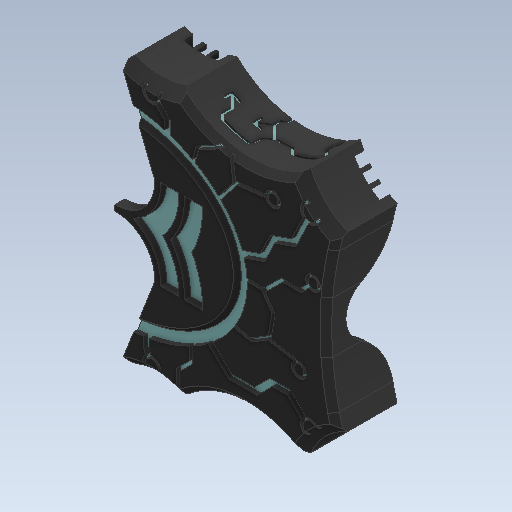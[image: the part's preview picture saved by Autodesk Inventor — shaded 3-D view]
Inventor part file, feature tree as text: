
AUTODESK INVENTOR PART (.ipt)
format: ipt  version: 2020 (Build 240168000, 168)  size: 1,965,056 bytes
history: native  units: mm
features: reference x74, projected_geometry x20, sketch x19, extrude x17, plane x6, other x6, fillet x5, chamfer x5, mirror x2, emboss x2
ambient origin geometry x8: Origin, YZ Plane, XZ Plane, XY Plane, X Axis, Y Axis, Z Axis, Center Point
bodies: Solid1 (feature_tree)
feature tree (156):
  extrude  "Extrusion1"  Depth=70.0mm
  extrude  "Extrusion4"  Depth=29.189217mm
  extrude  "Extrusion7"  Depth=20.0mm TaperAngle=0.0deg
  extrude  "Extrusion8"  Depth=36.552mm TaperAngle=0.0deg
  extrude  "Extrusion9"  Depth=20.0mm
  plane  "Work Plane2"
  mirror  "Mirror1"
  extrude  "Extrusion10"  Depth=26.0mm
  fillet  "Fillet3"  Radius=15.25mm
  fillet  "Fillet4"  Radius=35.5mm
  plane  "Work Plane3"
  extrude  "Extrusion11"  Depth=26.5mm TaperAngle=0.0deg
  plane  "Work Plane4"
  extrude  "Extrusion12"  Depth=46.75mm
  plane  "Work Plane5"
  extrude  "Extrusion14"  Depth=1.6mm TaperAngle=0.0deg
  fillet  "Fillet5"  Radius=78.75mm
  fillet  "Fillet6"  Radius=3.0mm
  fillet  "Fillet8"  Radius=5.0mm
  extrude  "Extrusion15"  Depth=8.0mm TaperAngle=0.0deg
  plane  "Work Plane6"
  extrude  "Extrusion17"  Depth=5.6mm
  emboss  "Emboss1"
  chamfer  "Chamfer3"  Distance=2.0mm
  chamfer  "Chamfer4"  Distance=12.25mm
  extrude  "Extrusion18"  Depth=2.0mm
  extrude  "Extrusion19"  Depth=45.0mm
  extrude  "Extrusion20"  Depth=50.0mm
  extrude  "Extrusion21"  Depth=2.0mm TaperAngle=0.0deg
  chamfer  "Chamfer5"  Distance=7.0mm
  extrude  "Extrusion22"  Depth=7.0mm
  extrude  "Extrusion23"  Depth=7.0mm
  chamfer  "Chamfer8"  Distance=7.0mm
  plane  "Work Plane8"
  emboss  "Emboss5"
  mirror  "Mirror2"
  chamfer  "Chamfer9"  Distance=9.5mm
  sketch  "Sketch1"  dims[d0=10.0mm d1=0.0mm d6=70.0mm]
  reference  "Reference1"
  reference  "Reference2"
  reference  "Reference3"
  reference  "Reference4"
  reference  "Reference5"
  reference  "Reference6"
  reference  "Reference7"
  reference  "Reference8"
  reference  "Reference9"
  reference  "Reference10"
  reference  "Reference11"
  reference  "Reference12"
  reference  "Reference13"
  reference  "Reference14"
  reference  "Reference15"
  reference  "Reference16"
  reference  "Reference17"
  reference  "Reference18"
  reference  "Reference19"
  reference  "Reference20"
  reference  "Reference21"
  reference  "Reference22"
  reference  "Reference23"
  reference  "Reference24"
  reference  "Reference25"
  reference  "Reference26"
  reference  "Reference27"
  reference  "Reference28"
  reference  "Reference29"
  reference  "Reference30"
  reference  "Reference31"
  reference  "Reference32"
  reference  "Reference33"
  reference  "Reference34"
  reference  "Reference35"
  reference  "Reference36"
  reference  "Reference37"
  reference  "Reference38"
  reference  "Reference39"
  reference  "Reference40"
  reference  "Reference41"
  reference  "Reference42"
  reference  "Reference43"
  reference  "Reference44"
  reference  "Reference45"
  reference  "Reference46"
  reference  "Reference47"
  reference  "Reference48"
  reference  "Reference49"
  reference  "Reference50"
  reference  "Reference51"
  reference  "Reference52"
  reference  "Reference53"
  reference  "Reference54"
  reference  "Reference55"
  reference  "Reference56"
  reference  "Reference57"
  reference  "Reference58"
  reference  "Reference59"
  reference  "Reference60"
  reference  "Reference61"
  reference  "Reference62"
  sketch  "Sketch5"  dims[d7=29.189217mm d8=29.189217mm]
  sketch  "Sketch8"  dims[d9=5.0mm d10=0.0mm d21=20.0mm d22=0.0mm]
  projected_geometry  "Projected Loop39"
  sketch  "Sketch9"  dims[d23=4.0mm d24=0.0mm d25=36.552mm d26=0.0mm]
  reference  "Reference110"
  projected_geometry  "Projected Loop40"
  sketch  "Sketch10"  dims[d27=10.0mm d28=20.0mm]
  projected_geometry  "Projected Loop41"
  sketch  "Sketch11"  dims[d29=20.0mm d30=0.0mm d31=26.0mm d32=15.25mm d33=35.5mm d34=0.0mm]
  projected_geometry  "Projected Loop42"
  sketch  "Sketch12"  dims[d35=5.0mm d36=0.0mm d39=26.5mm d40=0.0mm]
  reference  "Reference111"
  reference  "Reference112"
  reference  "Reference113"
  sketch  "Sketch14"  dims[d41=26.0mm d42=46.75mm]
  projected_geometry  "Projected Loop43"
  projected_geometry  "Projected Loop44"
  sketch  "Sketch16"  dims[d44=5.0mm d45=1.6mm d46=0.0mm d250=78.75mm d251=0.0mm d253=3.0mm d254=0.0mm]
  sketch  "Sketch17"  dims[d255=3.0mm d256=2.0mm d257=45.0deg]
  reference  "Reference114"
  reference  "Reference115"
  reference  "Reference116"
  reference  "Reference117"
  reference  "Reference118"
  reference  "Reference119"
  reference  "Reference120"
  reference  "Reference121"
  sketch  "Sketch19"  dims[d258=5.0mm d259=2.0mm d260=45.0deg]
  sketch  "Sketch22"  dims[d261=10.0mm d262=87.0mm d263=0.0mm d264=0.0mm d265=5.0mm]
  sketch  "Sketch23"  dims[d266=8.0mm d267=8.0mm d268=0.0mm]
  projected_geometry  "Projected Loop51"
  projected_geometry  "Projected Loop52"
  projected_geometry  "Projected Loop53"
  projected_geometry  "Projected Loop54"
  projected_geometry  "Projected Loop55"
  projected_geometry  "Projected Loop56"
  projected_geometry  "Projected Loop57"
  projected_geometry  "Projected Loop58"
  sketch  "Sketch24"  dims[d269=5.6mm d270=5.6mm d271=2.0mm d272=0.0mm]
  projected_geometry  "Projected Loop59"
  sketch  "Sketch25"  dims[d273=3.0mm]
  projected_geometry  "Projected Loop60"
  projected_geometry  "Projected Loop61"
  sketch  "Sketch26"  dims[d274=3.0mm d275=12.25mm d276=0.0mm]
  sketch  "Sketch27"  dims[d277=2.0mm d278=2.0mm d279=45.0deg d280=2.0mm]
  projected_geometry  "Projected Loop62"
  sketch  "Sketch28"  dims[d281=60.0mm d282=45.0mm]
  projected_geometry  "Projected Loop63"
  sketch  "Sketch31"  dims[d283=65.0mm d284=50.0mm d285=2.0mm d286=0.0mm d287=7.0mm d288=7.0mm d289=7.0mm d290=7.0mm d291=9.5mm d292=9.5mm d293=9.5mm d294=9.5mm d297=135.0deg d298=135.0deg d299=135.0deg d300=1.5mm d301=1.5mm d302=135.0deg d303=135.0deg d304=135.0deg d305=135.0deg d306=135.0deg d308=1.5mm d309=1.5mm d310=27.646716mm d311=1.5mm d312=1.5mm d313=1.5mm d314=1.5mm d315=135.0deg d316=135.0deg d317=135.0deg d318=90.0deg d319=135.0deg d320=1.5mm d322=135.0deg d323=1.5mm d324=1.5mm d325=1.5mm d326=135.0deg d327=135.0deg d328=1.5mm d329=135.0deg d330=1.5mm d331=135.0deg d332=1.5mm d333=5.0mm d334=7.5mm d335=5.0mm d336=7.5mm d337=0.799818mm d338=9.825599mm d339=4.886306mm d340=6.517162mm d341=6.977452mm d342=27.715251mm d343=75.147313mm d344=6.5832mm d345=38.018296mm d346=20.561417mm d347=21.837746mm d348=106.12207mm d349=130.123966mm d350=156.24898mm d351=80.618402mm d352=11.756867mm d353=85.385613mm d354=50.089279mm d355=183.080269mm d356=181.417126mm d357=179.402612mm d358=106.149833mm d359=65.180347mm d360=77.013159mm d361=68.583576mm d362=42.88392mm d363=200.478543mm d364=149.75924mm d365=229.704039mm d366=228.560976mm d367=127.436548mm d368=240.015033mm d369=49.64603mm d370=83.037972mm d371=81.829735mm d372=46.655621mm d373=51.006521mm d375=42.84284mm d377=30.283586mm d378=28.338533mm d379=32.281871mm d380=37.157053mm d381=13.389715mm d382=10.627147mm d383=2.168336mm d384=31.542813mm d385=30.334576mm d386=5.133293mm d387=23.300515mm d388=25.240716mm d389=17.601115mm d390=20.398023mm d391=13.462282mm d392=30.571818mm d393=7.221457mm d394=31.782295mm d395=11.262731mm d396=4.400575mm d397=5.0mm d398=7.5mm d399=10.655943mm d400=9.591201mm d401=180.0deg d402=2.0mm d403=0.0mm d415=2.0mm d416=2.0mm d417=45.0deg d418=5.930716mm d419=4.0mm d420=27.445097mm d421=2.0mm d422=135.0deg d423=135.0deg d424=135.0deg d425=3.0mm d426=2.0mm d427=4.0mm d428=1.5mm d429=135.0deg d430=135.0deg d431=5.0mm d432=2.0mm d433=1.5mm d434=3.5mm d435=1.5mm d436=3.5mm d437=1.5mm d438=2.0mm d439=1.5mm d441=1.5mm d442=135.0deg d443=135.0deg d444=1.5mm d445=1.5mm d446=4.0mm d447=90.0deg d448=1.5mm d458=1.106218mm d459=1.5mm d460=135.0deg d463=1.5mm d464=4.0mm d465=1.5mm d466=2.0mm d467=135.0deg d468=6.0mm d469=8.0mm d470=3.0mm d471=135.0deg d472=1.5mm d473=5.0mm d474=4.0mm d476=2.0mm d477=1.5mm d478=3.5mm d479=1.5mm d480=135.0deg d481=3.5mm d482=1.5mm d483=1.5mm d484=1.5mm d485=1.5mm d486=1.0mm d487=0.0mm d488=2.0mm d489=2.0mm d490=45.0deg d2=0.5mm d3=0.872665mm d4=0.5mm d5=0.872665mm]
  projected_geometry  "Projected Loop64"
  parser-record x2  (decoder bookkeeping rows leaked as tree rows — omitted from the tree; the rows remain in map.json)
  other  "Assembly1.iam"
  other  "BodyTest2:1"
  other  "BodyBot:1"
  other  "BodyMid:1"
note: 2 file-system paths scrubbed to <path> (originals preserved in map.json)
